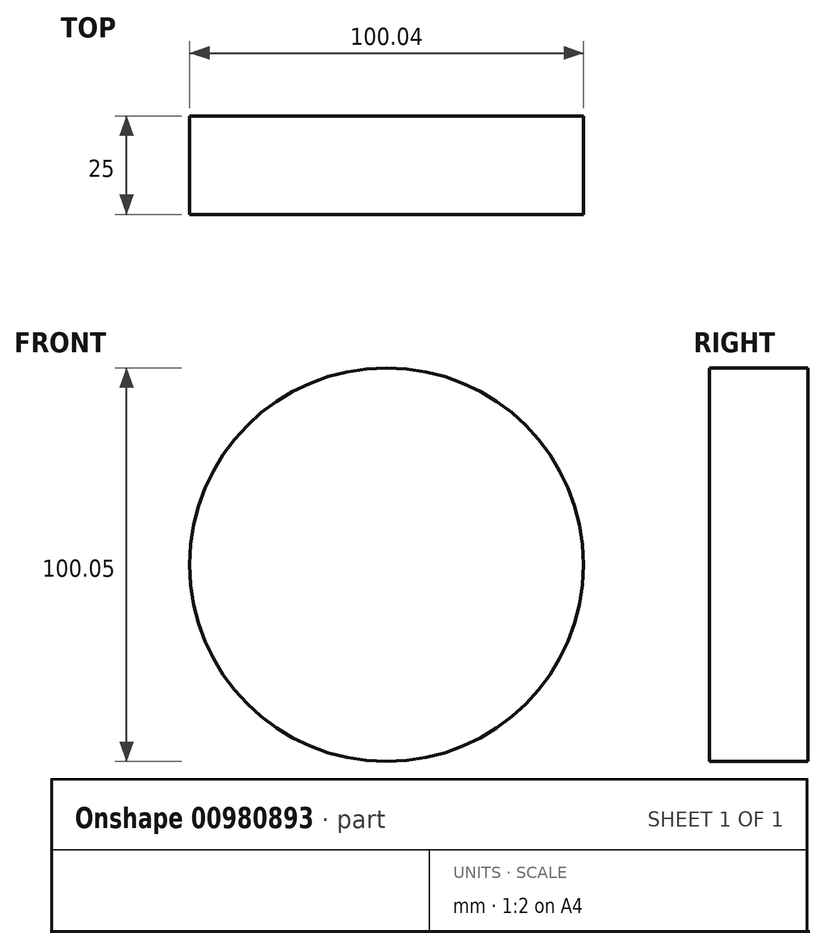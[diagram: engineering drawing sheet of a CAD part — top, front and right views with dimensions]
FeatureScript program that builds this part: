
annotation { "Feature Type Name" : "Feature", "Feature Type Description" : "" }
export const myFeature = defineFeature(function(context is Context, id is Id, definition is map)
    precondition{}
    {
        {
            var Q0;
            Q0=qCreatedBy(makeId("Front.planeOp"),FACE);
            var sketch = newSketch(context, id + "F0", { "sketchPlane" : qUnion([Q0])});
            skCircle(sketch, "E0", {"center": v(-79.05, 12.98) * mm, "radius": 50.02 * mm});
            skSolve(sketch);
        }
        {
            var Q0;
            Q0 = qSketchRegion(id + "F0", true);
            extrude(context, id + "F1", {"entities" : qUnion([Q0]), "depth" : 25 * mm, "offsetDistance" : 25 * mm});
        }
    });
